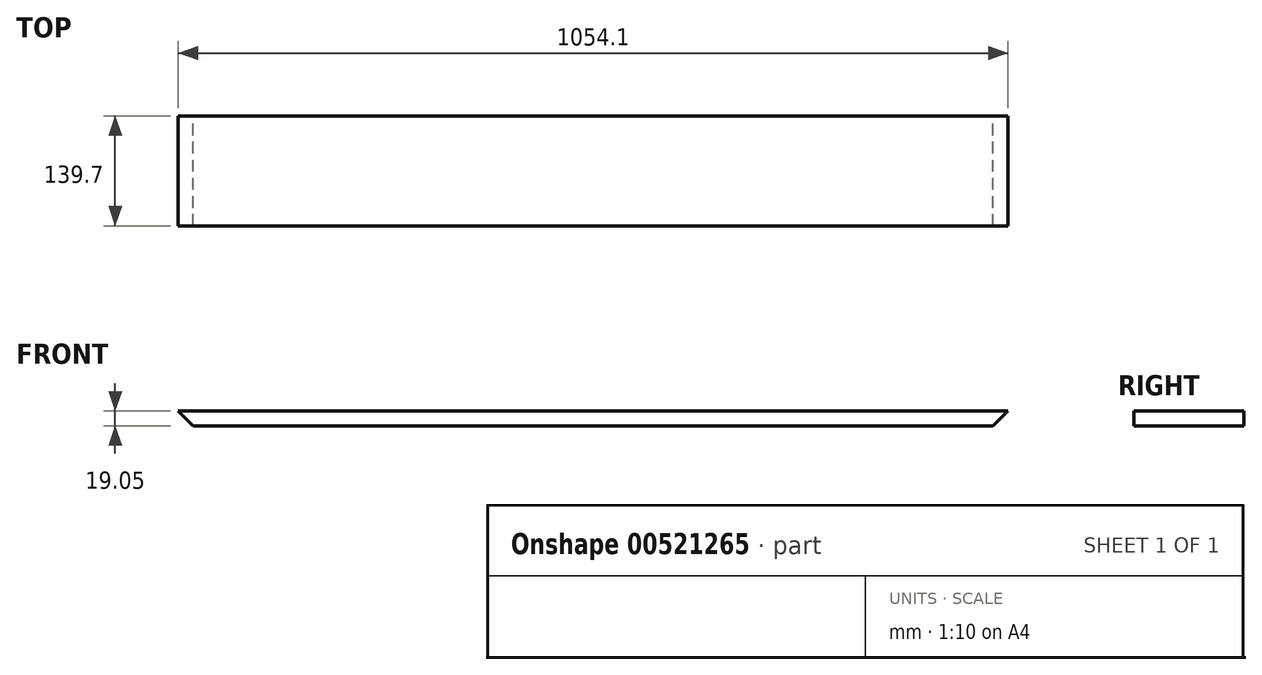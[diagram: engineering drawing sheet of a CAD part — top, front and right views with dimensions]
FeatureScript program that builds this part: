
annotation { "Feature Type Name" : "Feature", "Feature Type Description" : "" }
export const myFeature = defineFeature(function(context is Context, id is Id, definition is map)
    precondition{}
    {
        {
            var Q0;
            Q0=qCreatedBy(makeId("Front.planeOp"),FACE);
            var sketch = newSketch(context, id + "F0", { "sketchPlane" : qUnion([Q0])});
            skLineSegment(sketch, "E0", {"start": v(-508, 0) * mm, "end": v(-527.05, 19.05) * mm});
            skLineSegment(sketch, "E1", {"start": v(-527.05, 19.05) * mm, "end": v(527.05, 19.05) * mm});
            skLineSegment(sketch, "E2", {"start": v(527.05, 19.05) * mm, "end": v(508, 0) * mm});
            skLineSegment(sketch, "E3", {"start": v(508, 0) * mm, "end": v(-508, 0) * mm});
            skLineSegment(sketch, "E4", {"start": v(0, 570.25) * mm, "end": v(0, -656.25) * mm});
            skLineSegment(sketch, "E5", {"start": v(-542.33, 0) * mm, "end": v(651.2, 0) * mm});
            skSolve(sketch);
        }
        {
            var Q0;
            {var subQ0=sQuery(id+"F0.wireOp",EDGE,"E2");Q0=makeQuery(id+"F0.imprint","IMPRINT",FACE,{"disambiguationData":[TD([[makeQuery(id+"F0.imprint","IMPRINT",EDGE,{"derivedFrom":subQ0}),-1.0]])]});}
            var Q1;
            {var subQ0=sQuery(id+"F0.wireOp",EDGE,"E0");Q1=makeQuery(id+"F0.imprint","IMPRINT",FACE,{"disambiguationData":[TD([[makeQuery(id+"F0.imprint","IMPRINT",EDGE,{"derivedFrom":subQ0}),-1.0]])]});}
            extrude(context, id + "F1", {"entities" : qUnion([Q0, Q1]), "depth" : 139.7 * mm, "offsetDistance" : 25.4 * mm});
        }
    });
